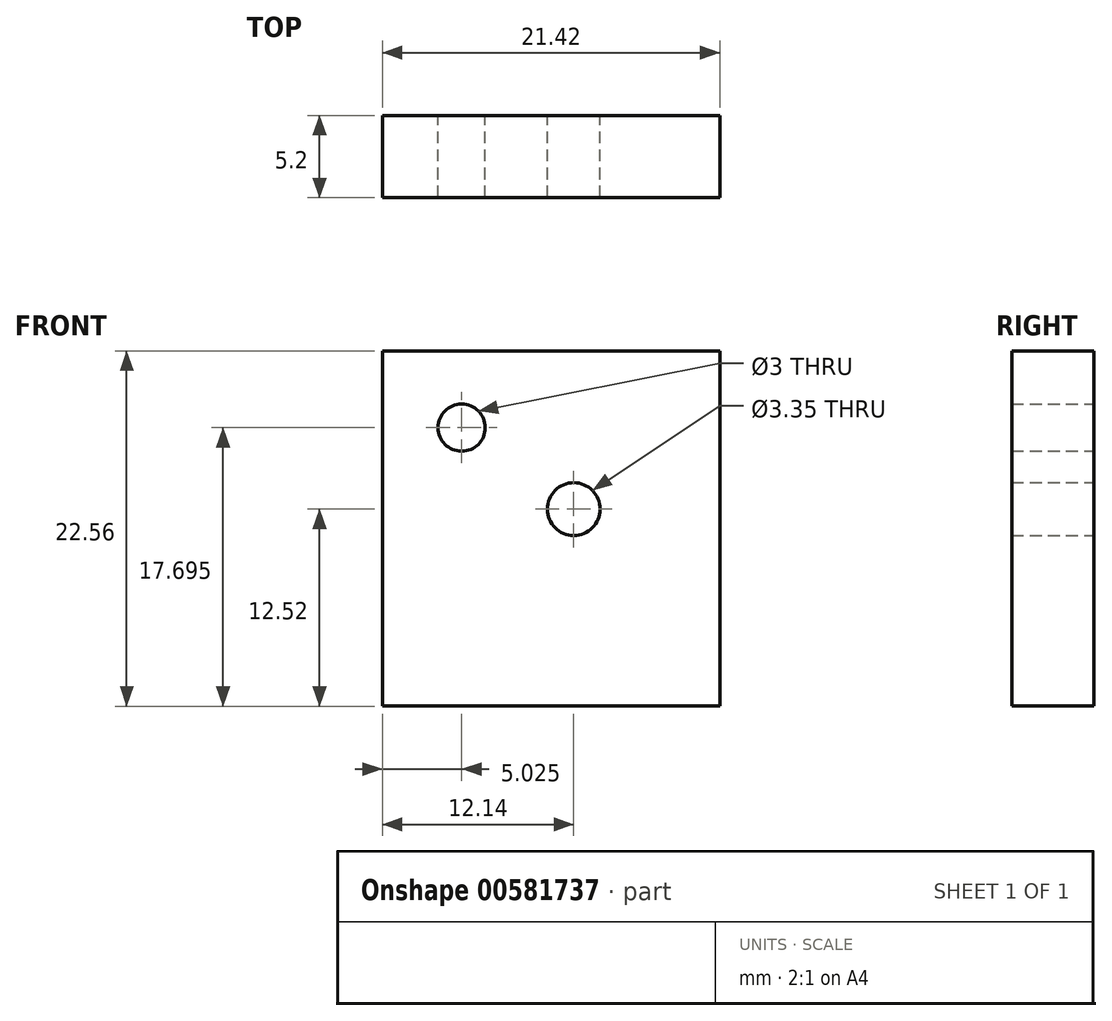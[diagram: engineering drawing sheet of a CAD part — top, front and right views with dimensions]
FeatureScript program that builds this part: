
annotation { "Feature Type Name" : "Feature", "Feature Type Description" : "" }
export const myFeature = defineFeature(function(context is Context, id is Id, definition is map)
    precondition{}
    {
        {
            var Q0;
            Q0=qCreatedBy(makeId("Front.planeOp"),FACE);
            var sketch = newSketch(context, id + "F0", { "sketchPlane" : qUnion([Q0])});
            skLineSegment(sketch, "E0.bottom", {"start": v(10.72, -11.28) * mm, "end": v(-10.71, -11.28) * mm});
            skLineSegment(sketch, "E0.top", {"start": v(10.71, 11.28) * mm, "end": v(-10.72, 11.27) * mm});
            skLineSegment(sketch, "E0.left", {"start": v(10.72, -11.28) * mm, "end": v(10.71, 11.28) * mm});
            skLineSegment(sketch, "E0.right", {"start": v(-10.71, -11.28) * mm, "end": v(-10.72, 11.27) * mm});
            skPoint(sketch, "E0.middle", {"position": v(0, 0) * mm});
            skCircle(sketch, "E1", {"center": v(-5.69, 6.42) * mm, "radius": 1.5 * mm});
            skCircle(sketch, "E2", {"center": v(1.43, 1.24) * mm, "radius": 1.68 * mm});
            skSolve(sketch);
        }
        {
            var Q0;
            Q0=makeQuery(id+"F0.imprint","IMPRINT",FACE,{"disambiguationData":[TD([[makeQuery(id+"F0.imprint","IMPRINT",EDGE,{"derivedFrom":sQuery(id+"F0.wireOp",EDGE,"E0.bottom")}),-1.0]])]});
            extrude(context, id + "F1", {"entities" : qUnion([Q0]), "depth" : 5.2 * mm, "offsetDistance" : 25 * mm});
        }
    });
